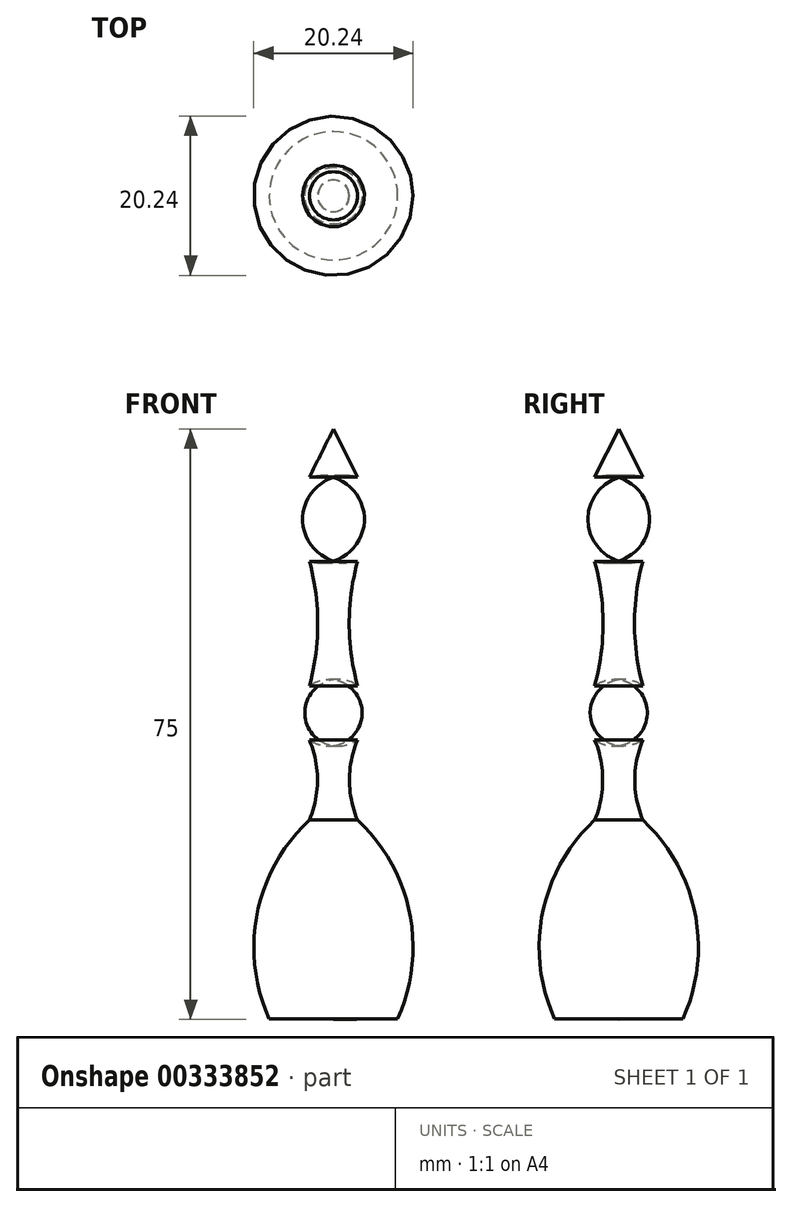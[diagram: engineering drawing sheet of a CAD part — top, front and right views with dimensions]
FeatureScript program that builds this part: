
annotation { "Feature Type Name" : "Feature", "Feature Type Description" : "" }
export const myFeature = defineFeature(function(context is Context, id is Id, definition is map)
    precondition{}
    {
        {
            var Q0;
            Q0=qCreatedBy(makeId("Front.planeOp"),FACE);
            var sketch = newSketch(context, id + "F0", { "sketchPlane" : qUnion([Q0])});
            skLineSegment(sketch, "E0", {"start": v(0, 0) * mm, "end": v(0, -75) * mm});
            skLineSegment(sketch, "E1", {"start": v(0, 0) * mm, "end": v(3.06, -6.12) * mm});
            skArc(sketch, "E2", {"start": v(3.06, -16.82) * mm, "mid": v(7.16, -11.47) * mm, "end": v(3.06, -6.12) * mm});
            skArc(sketch, "E3", {"start": v(3.06, -16.82) * mm, "mid": v(2, -24.72) * mm, "end": v(3.06, -32.62) * mm});
            skArc(sketch, "E4", {"start": v(3.06, -39.5) * mm, "mid": v(4.83, -36.06) * mm, "end": v(3.06, -32.62) * mm});
            skArc(sketch, "E5", {"start": v(3.06, -39.5) * mm, "mid": v(2.04, -44.6) * mm, "end": v(3.06, -49.69) * mm});
            skArc(sketch, "E6", {"start": v(8.15, -74.91) * mm, "mid": v(9.68, -61.48) * mm, "end": v(3.06, -49.69) * mm});
            skLineSegment(sketch, "E7", {"start": v(8.15, -74.91) * mm, "end": v(0, -75) * mm});
            skSolve(sketch);
        }
        {
            var Q0;
            Q0=makeQuery(id+"F0.imprint","IMPRINT",FACE,{"disambiguationData":[TD([[makeQuery(id+"F0.imprint","IMPRINT",EDGE,{"derivedFrom":sQuery(id+"F0.wireOp",EDGE,"E0")}),1.0]])]});
            var Q1;
            Q1=sQuery(id+"F0.wireOp",EDGE,"E0");
            revolve(context, id + "F1", {"entities" : qUnion([Q0]), "axis" : qUnion([Q1]), "revolveType" : RevolveType.FULL});
        }
    });
